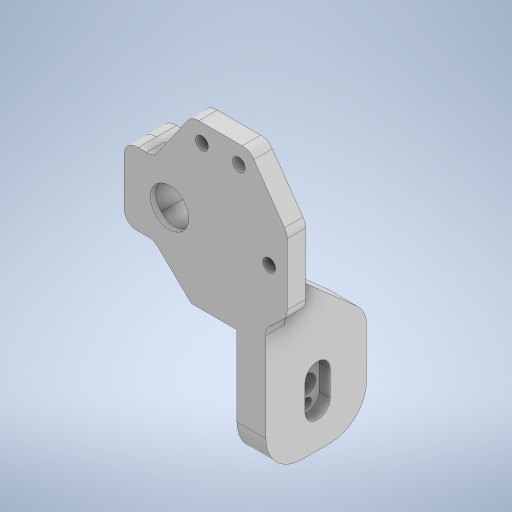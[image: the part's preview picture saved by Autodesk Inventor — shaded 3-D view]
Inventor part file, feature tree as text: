
AUTODESK INVENTOR PART (.ipt)
format: ipt  version: 2024.1 (Build 281209000, 209)  size: 475,648 bytes
history: native  units: in
note: dims shown in document units (in); Inventor stores cm internally (conversion verified against a paired STEP export)
features: extrude x7, fillet x7, sketch x7, direct_edit x1, other x1
ambient origin geometry x8: Origin, YZ Plane, XZ Plane, XY Plane, X Axis, Y Axis, Z Axis, Center Point
bodies: Solid1 (feature_tree)
feature tree (23):
  extrude  "Extrusion1"  Depth=0.8589in
  fillet  "Fillet1"  Radius=18.1102in
  extrude  "Extrusion2"  Depth=8.2677in
  fillet  "Fillet2"  Radius=20.0787in
  extrude  "Extrusion3"  Depth=4.3307in
  extrude  "Extrusion4"  Depth=5.1181in
  extrude  "Extrusion5"  Depth=4.9213in
  fillet  "Fillet3"  Radius=3.5433in
  fillet  "Fillet4"  Radius=3.5433in
  fillet  "Fillet5"  Radius=10.6299in
  fillet  "Face Fillet1"
  fillet  "Face Fillet2"
  extrude  "Extrusion6"  Depth=12.5984in
  extrude  "Extrusion7"  Depth=0.3937in
  direct_edit  "Direct Edit1"
  sketch  "Sketch1"  dims[d0=16.1417in d2=0.8589in d3=18.1102in]
  sketch  "Sketch2"  dims[d4=0.8589in d5=8.2677in d6=20.0787in]
  sketch  "Sketch3"  dims[d7=8.2677in d11=4.3307in]
  sketch  "Sketch4"  dims[d16=0.9201in d17=5.1181in]
  sketch  "Sketch5"  dims[d18=5.1181in d19=4.9213in d20=3.5433in d21=3.5433in d22=10.6299in]
  sketch  "Sketch6"  dims[d23=10.0394in d24=12.5984in]
  sketch  "Sketch7"  dims[d25=3.5433in d26=4.9213in d27=5.1181in d28=0.0in d29=3.937in d30=35.0394in d31=20.0787in d32=6.0039in d33=3.5433in d34=23.0315in d35=12.9921in d36=5.5in d37=0.0in d38=3.937in d39=3.622in d40=0.0in d41=2.0079in d42=2.0079in d43=3.002in d44=3.002in d45=7.0in d46=0.0in d47=42.126in d48=27.9528in d49=26.8504in d50=8.0236in d51=0.0in d52=10.0394in d53=7.874in d54=7.874in d55=7.874in d56=3.937in d57=3.937in d58=7.0in d59=7.0in d60=10.9055in d61=14.3307in d62=3.0in d63=0.0in d64=5.0in d65=2.5984in d66=2.5984in d67=4.4992in d68=4.4992in d69=0.0in d70=0.0in d71=0.0394in d72=0.3937in d73=0.3937in]
  other  "Scale1"
